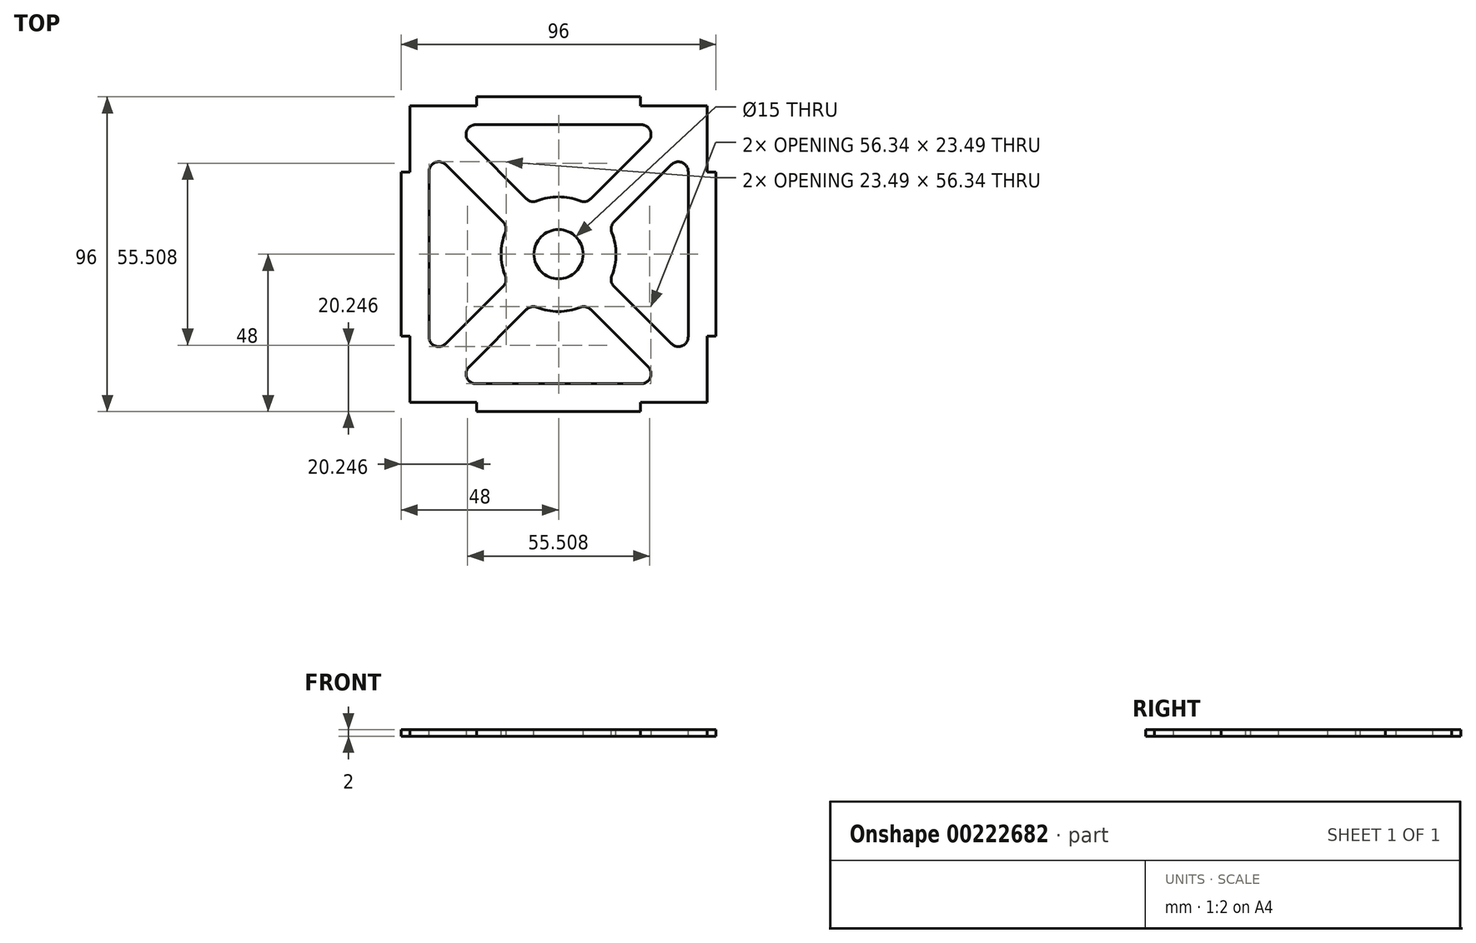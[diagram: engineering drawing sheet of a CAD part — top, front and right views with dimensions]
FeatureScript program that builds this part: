
annotation { "Feature Type Name" : "Feature", "Feature Type Description" : "" }
export const myFeature = defineFeature(function(context is Context, id is Id, definition is map)
    precondition{}
    {
        {
            var Q0;
            Q0=qCreatedBy(makeId("Top.planeOp"),FACE);
            var sketch = newSketch(context, id + "F0", { "sketchPlane" : qUnion([Q0])});
            skLineSegment(sketch, "E0.bottom", {"start": v(-45.25, 45.25) * mm, "end": v(-25, 45.25) * mm, "construction": true});
            skLineSegment(sketch, "E0.top", {"start": v(-45.25, -45.25) * mm, "end": v(-25, -45.25) * mm, "construction": true});
            skLineSegment(sketch, "E0.left", {"start": v(-45.25, 45.25) * mm, "end": v(-45.25, 25) * mm, "construction": true});
            skLineSegment(sketch, "E0.right", {"start": v(45.25, 45.25) * mm, "end": v(45.25, 25) * mm, "construction": true});
            skPoint(sketch, "E0.middle", {"position": v(0, 0) * mm});
            skLineSegment(sketch, "E1.top", {"start": v(25, 48) * mm, "end": v(-25, 48) * mm});
            skLineSegment(sketch, "E1.left", {"start": v(25, 45.25) * mm, "end": v(25, 48) * mm});
            skLineSegment(sketch, "E1.right", {"start": v(-25, 45.25) * mm, "end": v(-25, 48) * mm});
            skPoint(sketch, "E1.middle", {"position": v(0, 46.63) * mm});
            skPoint(sketch, "E1.middle.positionSnap0", {"position": v(0, 45.25) * mm});
            skPoint(sketch, "E1.centerSnap0", {"position": v(0, 45.25) * mm});
            skLineSegment(sketch, "E2.bottom", {"start": v(45.25, 25) * mm, "end": v(48, 25) * mm});
            skLineSegment(sketch, "E2.top", {"start": v(45.25, -25) * mm, "end": v(48, -25) * mm});
            skLineSegment(sketch, "E2.right", {"start": v(48, 25) * mm, "end": v(48, -25) * mm});
            skPoint(sketch, "E2.middle", {"position": v(46.63, 0) * mm});
            skLineSegment(sketch, "E3", {"start": v(0, 45.25) * mm, "end": v(0, -45.25) * mm, "construction": true});
            skLineSegment(sketch, "E4", {"start": v(-45.25, 0) * mm, "end": v(46.63, 0) * mm, "construction": true});
            skLineSegment(sketch, "E5.MirrorCS", {"start": v(-45.25, 25) * mm, "end": v(-48, 25) * mm});
            skLineSegment(sketch, "E6.MirrorCS", {"start": v(-45.25, -25) * mm, "end": v(-48, -25) * mm});
            skLineSegment(sketch, "E7.MirrorCS", {"start": v(-48, 25) * mm, "end": v(-48, -25) * mm});
            skPoint(sketch, "E8.MirrorP", {"position": v(-46.62, 0) * mm});
            skLineSegment(sketch, "E9.MirrorCS", {"start": v(-25, -45.25) * mm, "end": v(-25, -48) * mm});
            skLineSegment(sketch, "E10.MirrorCS", {"start": v(25, -45.25) * mm, "end": v(25, -48) * mm});
            skPoint(sketch, "E11.MirrorP", {"position": v(0, -45.25) * mm});
            skPoint(sketch, "E12.MirrorP", {"position": v(0, -46.63) * mm});
            skLineSegment(sketch, "E13.MirrorCS", {"start": v(25, -48) * mm, "end": v(-25, -48) * mm});
            skLineSegment(sketch, "E14.trimOffspring", {"start": v(-45.25, -25) * mm, "end": v(-45.25, -45.25) * mm, "construction": true});
            skLineSegment(sketch, "E15.trimOffspring", {"start": v(45.25, -25) * mm, "end": v(45.25, -45.25) * mm, "construction": true});
            skLineSegment(sketch, "E16.trimOffspring", {"start": v(25, -45.25) * mm, "end": v(45.25, -45.25) * mm, "construction": true});
            skLineSegment(sketch, "E17.trimOffspring", {"start": v(25, 45.25) * mm, "end": v(45.25, 45.25) * mm, "construction": true});
            skLineSegment(sketch, "E18", {"start": v(-25, 45.25) * mm, "end": v(-45.25, 45.25) * mm});
            skLineSegment(sketch, "E19", {"start": v(-45.25, 25) * mm, "end": v(-45.25, 45.25) * mm});
            skLineSegment(sketch, "E20", {"start": v(-45.25, -25) * mm, "end": v(-45.25, -45.25) * mm});
            skLineSegment(sketch, "E21", {"start": v(-45.25, -45.25) * mm, "end": v(-25, -45.25) * mm});
            skLineSegment(sketch, "E22", {"start": v(25, -45.25) * mm, "end": v(45.25, -45.25) * mm});
            skLineSegment(sketch, "E23", {"start": v(45.25, -25) * mm, "end": v(45.25, -45.25) * mm});
            skLineSegment(sketch, "E24", {"start": v(45.25, 45.25) * mm, "end": v(45.25, 25) * mm});
            skLineSegment(sketch, "E25", {"start": v(25, 45.25) * mm, "end": v(45.25, 45.25) * mm});
            skSolve(sketch);
        }
        {
            var Q0;
            Q0=makeQuery(id+"F0.imprint","IMPRINT",FACE,{"disambiguationData":[TD([[makeQuery(id+"F0.imprint","IMPRINT",EDGE,{"derivedFrom":sQuery(id+"F0.wireOp",EDGE,"E1.top")}),1.0]])]});
            extrude(context, id + "F1", {"entities" : qUnion([Q0]), "depth" : 2 * mm});
        }
        {
            var Q0;
            Q0=makeQuery(id+"F1.opExtrude","CAP_FACE",FACE,{"disambiguationData":[OSD([sQuery(id+"F0.wireOp",EDGE,"E1.top"),sQuery(id+"F0.wireOp",EDGE,"E1.left"),sQuery(id+"F0.wireOp",EDGE,"E1.right"),sQuery(id+"F0.wireOp",EDGE,"E2.bottom"),sQuery(id+"F0.wireOp",EDGE,"E2.top"),sQuery(id+"F0.wireOp",EDGE,"E2.right"),sQuery(id+"F0.wireOp",EDGE,"E5.MirrorCS"),sQuery(id+"F0.wireOp",EDGE,"E6.MirrorCS"),sQuery(id+"F0.wireOp",EDGE,"E7.MirrorCS"),sQuery(id+"F0.wireOp",EDGE,"E9.MirrorCS"),sQuery(id+"F0.wireOp",EDGE,"E10.MirrorCS"),sQuery(id+"F0.wireOp",EDGE,"E13.MirrorCS"),sQuery(id+"F0.wireOp",EDGE,"E18"),sQuery(id+"F0.wireOp",EDGE,"E19"),sQuery(id+"F0.wireOp",EDGE,"E20"),sQuery(id+"F0.wireOp",EDGE,"E21"),sQuery(id+"F0.wireOp",EDGE,"E22"),sQuery(id+"F0.wireOp",EDGE,"E23"),sQuery(id+"F0.wireOp",EDGE,"E24"),sQuery(id+"F0.wireOp",EDGE,"E25")])],"isStart":false});
            var sketch = newSketch(context, id + "F2", { "sketchPlane" : qUnion([Q0])});
            skCircle(sketch, "E26", {"center": v(0, 0) * mm, "radius": 7.5 * mm});
            skArc(sketch, "E27", {"start": v(-15.4, 8.32) * mm, "mid": v(-17.5, 0) * mm, "end": v(-15.4, -8.32) * mm});
            skLineSegment(sketch, "E28", {"start": v(0, 0) * mm, "end": v(-45.25, 45.25) * mm, "construction": true});
            skLineSegment(sketch, "E29", {"start": v(0, 0) * mm, "end": v(45.25, 45.25) * mm, "construction": true});
            skLineSegment(sketch, "E30", {"start": v(0, 0) * mm, "end": v(-45.25, -45.25) * mm, "construction": true});
            skLineSegment(sketch, "E31", {"start": v(0, 0) * mm, "end": v(45.25, -45.25) * mm, "construction": true});
            skLineSegment(sketch, "E32", {"start": v(-8.32, 15.4) * mm, "end": v(-32.43, 39.5) * mm});
            skLineSegment(sketch, "E33", {"start": v(-32.43, 39.5) * mm, "end": v(32.43, 39.5) * mm});
            skLineSegment(sketch, "E34", {"start": v(32.43, 39.5) * mm, "end": v(8.32, 15.4) * mm});
            skLineSegment(sketch, "E35", {"start": v(-15.4, 8.32) * mm, "end": v(-39.5, 32.43) * mm});
            skLineSegment(sketch, "E36", {"start": v(-39.5, 32.43) * mm, "end": v(-39.5, -32.43) * mm});
            skLineSegment(sketch, "E37", {"start": v(-39.5, -32.43) * mm, "end": v(-15.4, -8.32) * mm});
            skLineSegment(sketch, "E38", {"start": v(0, 0) * mm, "end": v(0, -48) * mm, "construction": true});
            skLineSegment(sketch, "E39", {"start": v(0, 0) * mm, "end": v(48, 0) * mm, "construction": true});
            skLineSegment(sketch, "E40.MirrorCS", {"start": v(32.43, -39.5) * mm, "end": v(8.32, -15.4) * mm});
            skLineSegment(sketch, "E41.MirrorCS", {"start": v(-32.43, -39.5) * mm, "end": v(32.43, -39.5) * mm});
            skLineSegment(sketch, "E42.MirrorCS", {"start": v(-8.32, -15.4) * mm, "end": v(-32.43, -39.5) * mm});
            skLineSegment(sketch, "E43.MirrorCS", {"start": v(-15.4, -8.32) * mm, "end": v(-39.5, -32.43) * mm});
            skLineSegment(sketch, "E44.MirrorCS", {"start": v(-39.5, -32.43) * mm, "end": v(-39.5, 32.43) * mm});
            skLineSegment(sketch, "E45.MirrorCS", {"start": v(15.4, -8.32) * mm, "end": v(39.5, -32.43) * mm});
            skLineSegment(sketch, "E46.MirrorCS", {"start": v(15.4, 8.32) * mm, "end": v(39.5, 32.43) * mm});
            skLineSegment(sketch, "E47.MirrorCS", {"start": v(39.5, 32.43) * mm, "end": v(39.5, -32.43) * mm});
            skArc(sketch, "E48.trimOffspring", {"start": v(8.32, 15.4) * mm, "mid": v(0, 17.5) * mm, "end": v(-8.32, 15.4) * mm});
            skArc(sketch, "E49.trimOffspring", {"start": v(15.4, -8.32) * mm, "mid": v(17.5, 0) * mm, "end": v(15.4, 8.32) * mm});
            skArc(sketch, "E50.trimOffspring", {"start": v(-8.32, -15.4) * mm, "mid": v(0, -17.5) * mm, "end": v(8.32, -15.4) * mm});
            skSolve(sketch);
        }
        {
            var Q0;
            Q0=makeQuery(id+"F2.imprint","IMPRINT",FACE,{"disambiguationData":[TD([[makeQuery(id+"F2.imprint","IMPRINT",EDGE,{"derivedFrom":sQuery(id+"F2.wireOp",EDGE,"E27")}),-1.0]])]});
            var Q1;
            Q1=makeQuery(id+"F2.imprint","IMPRINT",FACE,{"disambiguationData":[TD([[makeQuery(id+"F2.imprint","IMPRINT",EDGE,{"derivedFrom":sQuery(id+"F2.wireOp",EDGE,"E32")}),-1.0]])]});
            var Q2;
            Q2=makeQuery(id+"F2.imprint","IMPRINT",FACE,{"disambiguationData":[TD([[makeQuery(id+"F2.imprint","IMPRINT",EDGE,{"derivedFrom":sQuery(id+"F2.wireOp",EDGE,"E26")}),1.0]])]});
            var Q3;
            Q3=makeQuery(id+"F2.imprint","IMPRINT",FACE,{"disambiguationData":[TD([[makeQuery(id+"F2.imprint","IMPRINT",EDGE,{"derivedFrom":sQuery(id+"F2.wireOp",EDGE,"E45.MirrorCS")}),1.0]])]});
            var Q4;
            Q4=makeQuery(id+"F2.imprint","IMPRINT",FACE,{"disambiguationData":[TD([[makeQuery(id+"F2.imprint","IMPRINT",EDGE,{"derivedFrom":sQuery(id+"F2.wireOp",EDGE,"E40.MirrorCS")}),1.0]])]});
            extrude(context, id + "F3", {"entities" : qUnion([Q0, Q1, Q2, Q3, Q4]), "operationType" : NewBodyOperationType.REMOVE, "oppositeDirection" : true, "depth" : 25 * mm});
        }
        {
            var Q0;
            Q0=makeQuery(id+"F3.boolean.opBoolean","COPY",EDGE,{"derivedFrom":makeQuery(id+"F3.opExtrude","SWEPT_EDGE",EDGE,{"disambiguationData":[OSD([sQuery(id+"F2.wireOp",EDGE,"E35"),sQuery(id+"F2.wireOp",EDGE,"E36")])]})});
            var Q1;
            Q1=makeQuery(id+"F3.boolean.opBoolean","COPY",EDGE,{"derivedFrom":makeQuery(id+"F3.opExtrude","SWEPT_EDGE",EDGE,{"disambiguationData":[OSD([sQuery(id+"F2.wireOp",EDGE,"E27"),sQuery(id+"F2.wireOp",EDGE,"E43.MirrorCS")])]})});
            var Q2;
            Q2=makeQuery(id+"F3.boolean.opBoolean","COPY",EDGE,{"derivedFrom":makeQuery(id+"F3.opExtrude","SWEPT_EDGE",EDGE,{"disambiguationData":[OSD([sQuery(id+"F2.wireOp",EDGE,"E27"),sQuery(id+"F2.wireOp",EDGE,"E35")])]})});
            var Q3;
            Q3=makeQuery(id+"F3.boolean.opBoolean","COPY",EDGE,{"derivedFrom":makeQuery(id+"F3.opExtrude","SWEPT_EDGE",EDGE,{"disambiguationData":[OSD([sQuery(id+"F2.wireOp",EDGE,"E34"),sQuery(id+"F2.wireOp",EDGE,"E48.trimOffspring")])]})});
            var Q4;
            Q4=makeQuery(id+"F3.boolean.opBoolean","COPY",EDGE,{"derivedFrom":makeQuery(id+"F3.opExtrude","SWEPT_EDGE",EDGE,{"disambiguationData":[OSD([sQuery(id+"F2.wireOp",EDGE,"E32"),sQuery(id+"F2.wireOp",EDGE,"E48.trimOffspring")])]})});
            var Q5;
            Q5=makeQuery(id+"F3.boolean.opBoolean","COPY",EDGE,{"derivedFrom":makeQuery(id+"F3.opExtrude","SWEPT_EDGE",EDGE,{"disambiguationData":[OSD([sQuery(id+"F2.wireOp",EDGE,"E41.MirrorCS"),sQuery(id+"F2.wireOp",EDGE,"E42.MirrorCS")])]})});
            var Q6;
            Q6=makeQuery(id+"F3.boolean.opBoolean","COPY",EDGE,{"derivedFrom":makeQuery(id+"F3.opExtrude","SWEPT_EDGE",EDGE,{"disambiguationData":[OSD([sQuery(id+"F2.wireOp",EDGE,"E45.MirrorCS"),sQuery(id+"F2.wireOp",EDGE,"E49.trimOffspring")])]})});
            var Q7;
            Q7=makeQuery(id+"F3.boolean.opBoolean","COPY",EDGE,{"derivedFrom":makeQuery(id+"F3.opExtrude","SWEPT_EDGE",EDGE,{"disambiguationData":[OSD([sQuery(id+"F2.wireOp",EDGE,"E46.MirrorCS"),sQuery(id+"F2.wireOp",EDGE,"E49.trimOffspring")])]})});
            var Q8;
            Q8=makeQuery(id+"F3.boolean.opBoolean","COPY",EDGE,{"derivedFrom":makeQuery(id+"F3.opExtrude","SWEPT_EDGE",EDGE,{"disambiguationData":[OSD([sQuery(id+"F2.wireOp",EDGE,"E45.MirrorCS"),sQuery(id+"F2.wireOp",EDGE,"E47.MirrorCS")])]})});
            var Q9;
            Q9=makeQuery(id+"F3.boolean.opBoolean","COPY",EDGE,{"derivedFrom":makeQuery(id+"F3.opExtrude","SWEPT_EDGE",EDGE,{"disambiguationData":[OSD([sQuery(id+"F2.wireOp",EDGE,"E46.MirrorCS"),sQuery(id+"F2.wireOp",EDGE,"E47.MirrorCS")])]})});
            var Q10;
            Q10=makeQuery(id+"F3.boolean.opBoolean","COPY",EDGE,{"derivedFrom":makeQuery(id+"F3.opExtrude","SWEPT_EDGE",EDGE,{"disambiguationData":[OSD([sQuery(id+"F2.wireOp",EDGE,"E33"),sQuery(id+"F2.wireOp",EDGE,"E34")])]})});
            var Q11;
            Q11=makeQuery(id+"F3.boolean.opBoolean","COPY",EDGE,{"derivedFrom":makeQuery(id+"F3.opExtrude","SWEPT_EDGE",EDGE,{"disambiguationData":[OSD([sQuery(id+"F2.wireOp",EDGE,"E40.MirrorCS"),sQuery(id+"F2.wireOp",EDGE,"E41.MirrorCS")])]})});
            var Q12;
            Q12=makeQuery(id+"F3.boolean.opBoolean","COPY",EDGE,{"derivedFrom":makeQuery(id+"F3.opExtrude","SWEPT_EDGE",EDGE,{"disambiguationData":[OSD([sQuery(id+"F2.wireOp",EDGE,"E36"),sQuery(id+"F2.wireOp",EDGE,"E43.MirrorCS")])]})});
            var Q13;
            Q13=makeQuery(id+"F3.boolean.opBoolean","COPY",EDGE,{"derivedFrom":makeQuery(id+"F3.opExtrude","SWEPT_EDGE",EDGE,{"disambiguationData":[OSD([sQuery(id+"F2.wireOp",EDGE,"E32"),sQuery(id+"F2.wireOp",EDGE,"E33")])]})});
            var Q14;
            Q14=makeQuery(id+"F3.boolean.opBoolean","COPY",EDGE,{"derivedFrom":makeQuery(id+"F3.opExtrude","SWEPT_EDGE",EDGE,{"disambiguationData":[OSD([sQuery(id+"F2.wireOp",EDGE,"E42.MirrorCS"),sQuery(id+"F2.wireOp",EDGE,"E50.trimOffspring")])]})});
            var Q15;
            Q15=makeQuery(id+"F3.boolean.opBoolean","COPY",EDGE,{"derivedFrom":makeQuery(id+"F3.opExtrude","SWEPT_EDGE",EDGE,{"disambiguationData":[OSD([sQuery(id+"F2.wireOp",EDGE,"E40.MirrorCS"),sQuery(id+"F2.wireOp",EDGE,"E50.trimOffspring")])]})});
            fillet(context, id + "F4", {"entities" : qUnion([Q0, Q1, Q2, Q3, Q4, Q5, Q6, Q7, Q8, Q9, Q10, Q11, Q12, Q13, Q14, Q15]), "radius" : 3 * mm, "tangentPropagation" : true, "allowEdgeOverflow" : false});
        }
    });
